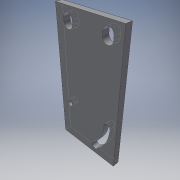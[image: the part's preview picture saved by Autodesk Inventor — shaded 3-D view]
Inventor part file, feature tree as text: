
AUTODESK INVENTOR PART (.ipt)
format: ipt  version: 2016 (Build 200138000, 138)  size: 146,432 bytes
history: native  units: mm
features: extrude x2, sketch x2, projected_geometry x1
ambient origin geometry x8: Origin, YZ Plane, XZ Plane, XY Plane, X Axis, Y Axis, Z Axis, Center Point
bodies: Solid1 (feature_tree)
feature tree (5):
  extrude  "Extrusion1"  Depth=40.0mm
  extrude  "Extrusion2"  Depth=10.0mm
  sketch  "Sketch1"  dims[d0=20.0mm d1=40.0mm]
  sketch  "Sketch2"  dims[d2=2.0mm d3=0.0mm d4=10.0mm d6=11.0mm d8=3.0mm d9=3.0mm d10=8.0mm d11=8.0mm d12=6.0mm d13=6.0mm d14=3.0mm d15=3.0mm d16=4.5mm d17=2.0mm d18=3.0mm d19=3.0mm d20=30.0mm d21=26.0mm d22=45.0deg d23=3.0mm d24=0.0mm]
  projected_geometry  "Projected Loop1"
